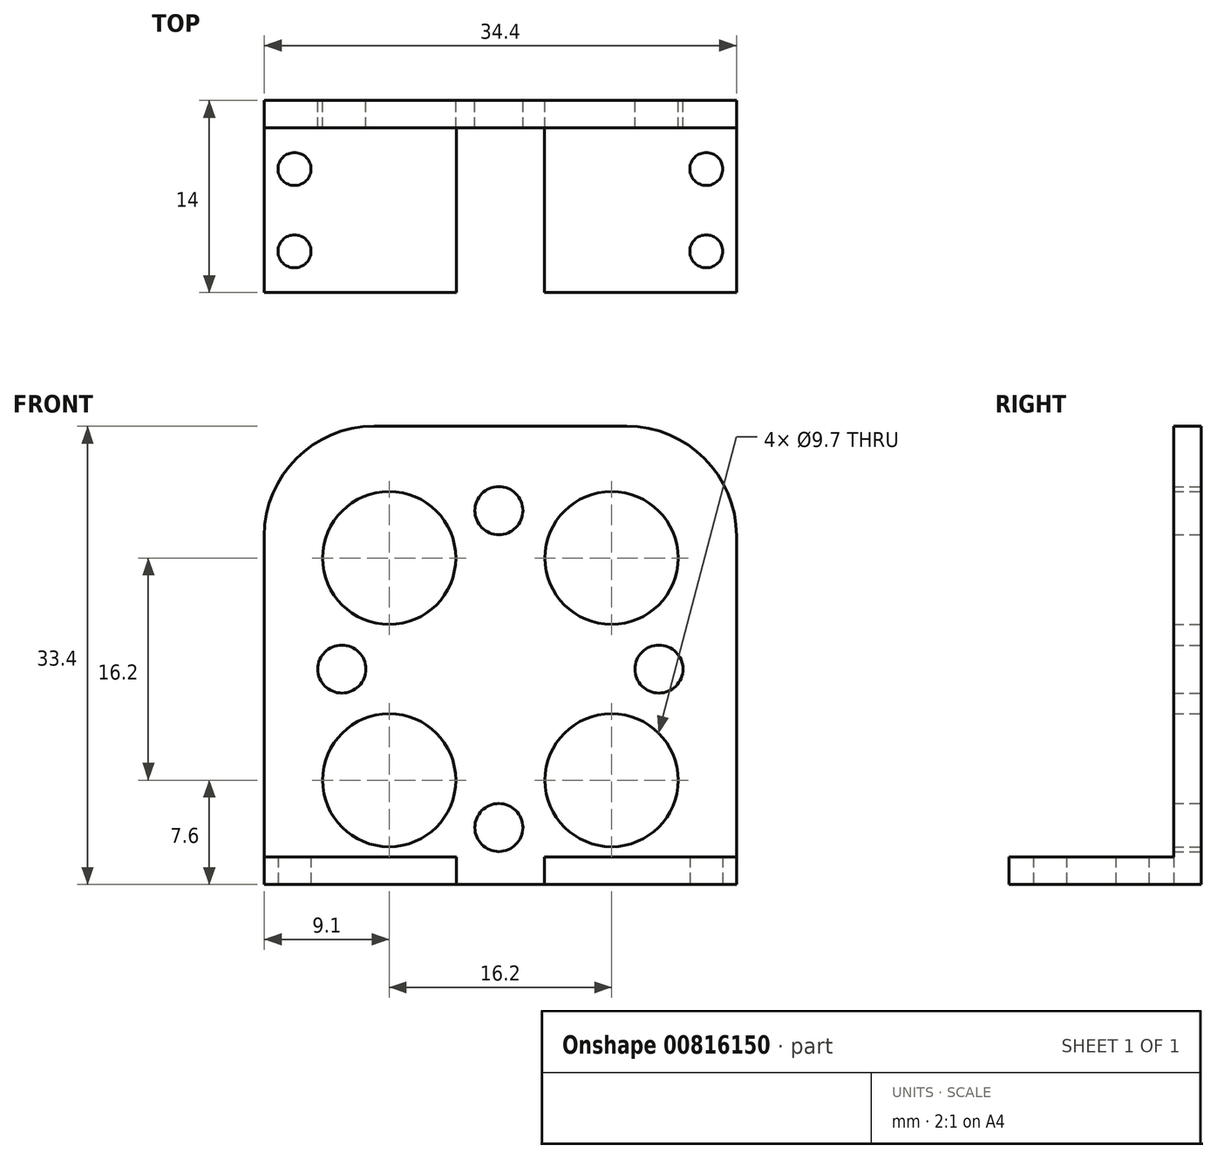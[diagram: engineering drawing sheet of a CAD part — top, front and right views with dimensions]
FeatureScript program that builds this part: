
annotation { "Feature Type Name" : "Feature", "Feature Type Description" : "" }
export const myFeature = defineFeature(function(context is Context, id is Id, definition is map)
    precondition{}
    {
        {
            var Q0;
            Q0=qCreatedBy(makeId("Front.planeOp"),FACE);
            var sketch = newSketch(context, id + "F0", { "sketchPlane" : qUnion([Q0])});
            skCircle(sketch, "E0", {"center": v(-0.11, 11.55) * mm, "radius": 1.75 * mm});
            skCircle(sketch, "E1", {"center": v(-11.55, 0) * mm, "radius": 1.75 * mm});
            skCircle(sketch, "E2", {"center": v(11.55, 0) * mm, "radius": 1.75 * mm});
            skCircle(sketch, "E3", {"center": v(-0.11, -11.55) * mm, "radius": 1.75 * mm});
            skLineSegment(sketch, "E4.bottom", {"start": v(-9.2, 17.7) * mm, "end": v(9.2, 17.7) * mm});
            skLineSegment(sketch, "E4.top", {"start": v(-17.2, -15.7) * mm, "end": v(17.2, -15.7) * mm});
            skLineSegment(sketch, "E4.left", {"start": v(-17.2, 9.7) * mm, "end": v(-17.2, -15.7) * mm});
            skLineSegment(sketch, "E4.right", {"start": v(17.2, 9.7) * mm, "end": v(17.2, -15.7) * mm});
            skCircle(sketch, "E5", {"center": v(-8.1, -8.1) * mm, "radius": 4.85 * mm});
            skCircle(sketch, "E6", {"center": v(-8.1, 8.1) * mm, "radius": 4.85 * mm});
            skCircle(sketch, "E7", {"center": v(8.1, 8.1) * mm, "radius": 4.85 * mm});
            skCircle(sketch, "E8", {"center": v(8.1, -8.1) * mm, "radius": 4.85 * mm});
            skPoint(sketch, "E9.visualSharp", {"position": v(-17.2, 17.7) * mm});
            skArc(sketch, "E9.filletArc", {"start": v(-9.2, 17.7) * mm, "mid": v(-14.86, 15.36) * mm, "end": v(-17.2, 9.7) * mm});
            skPoint(sketch, "E10.visualSharp", {"position": v(17.2, 17.7) * mm});
            skArc(sketch, "E10.filletArc", {"start": v(17.2, 9.7) * mm, "mid": v(14.86, 15.36) * mm, "end": v(9.2, 17.7) * mm});
            skSolve(sketch);
        }
        {
            var Q0;
            Q0=makeQuery(id+"F0.imprint","IMPRINT",FACE,{"disambiguationData":[TD([[makeQuery(id+"F0.imprint","IMPRINT",EDGE,{"derivedFrom":sQuery(id+"F0.wireOp",EDGE,"E0")}),-1.0]])]});
            var Q1;
            Q1 = qSketchRegion(id + "F2", true);
            extrude(context, id + "F1", {"entities" : qUnion([Q0, Q1]), "depth" : 2 * mm, "offsetDistance" : 25 * mm});
        }
        {
            var Q0;
            Q0=makeQuery(id+"F1.opExtrude","CAP_FACE",FACE,{"disambiguationData":[OSD([sQuery(id+"F0.wireOp",EDGE,"E0"),sQuery(id+"F0.wireOp",EDGE,"E1"),sQuery(id+"F0.wireOp",EDGE,"E2"),sQuery(id+"F0.wireOp",EDGE,"E3"),sQuery(id+"F0.wireOp",EDGE,"E4.bottom"),sQuery(id+"F0.wireOp",EDGE,"E4.top"),sQuery(id+"F0.wireOp",EDGE,"E4.left"),sQuery(id+"F0.wireOp",EDGE,"E4.right"),sQuery(id+"F0.wireOp",EDGE,"E5"),sQuery(id+"F0.wireOp",EDGE,"E6"),sQuery(id+"F0.wireOp",EDGE,"E7"),sQuery(id+"F0.wireOp",EDGE,"E8")])],"isStart":false});
            var sketch = newSketch(context, id + "F2", { "sketchPlane" : qUnion([Q0])});
            skLineSegment(sketch, "E11.bottom", {"start": v(-17.2, -13.7) * mm, "end": v(-3.2, -13.7) * mm});
            skLineSegment(sketch, "E11.top", {"start": v(-17.2, -15.7) * mm, "end": v(-3.2, -15.7) * mm});
            skLineSegment(sketch, "E11.left", {"start": v(-17.2, -13.7) * mm, "end": v(-17.2, -15.7) * mm});
            skLineSegment(sketch, "E11.right", {"start": v(-3.2, -13.7) * mm, "end": v(-3.2, -15.7) * mm});
            skLineSegment(sketch, "E12.bottom", {"start": v(17.2, -13.7) * mm, "end": v(3.2, -13.7) * mm});
            skLineSegment(sketch, "E12.top", {"start": v(17.2, -15.7) * mm, "end": v(3.2, -15.7) * mm});
            skLineSegment(sketch, "E12.left", {"start": v(17.2, -13.7) * mm, "end": v(17.2, -15.7) * mm});
            skLineSegment(sketch, "E12.right", {"start": v(3.2, -13.7) * mm, "end": v(3.2, -15.7) * mm});
            skSolve(sketch);
        }
        {
            var Q0;
            Q0=makeQuery(id+"F2.imprint","IMPRINT",FACE,{"disambiguationData":[TD([[makeQuery(id+"F2.imprint","IMPRINT",EDGE,{"derivedFrom":sQuery(id+"F2.wireOp",EDGE,"E11.bottom")}),-1.0]])]});
            var Q1;
            Q1=makeQuery(id+"F2.imprint","IMPRINT",FACE,{"disambiguationData":[TD([[makeQuery(id+"F2.imprint","IMPRINT",EDGE,{"derivedFrom":sQuery(id+"F2.wireOp",EDGE,"E12.bottom")}),1.0]])]});
            extrude(context, id + "F3", {"entities" : qUnion([Q0, Q1]), "operationType" : NewBodyOperationType.ADD, "depth" : 12 * mm, "offsetDistance" : 25 * mm});
        }
        {
            var Q0;
            Q0=makeQuery(id+"F3.boolean.opBoolean","MERGE",FACE,{"derivedFrom":[makeQuery(id+"F1.opExtrude","SWEPT_FACE",FACE,{"disambiguationData":[OSD([sQuery(id+"F0.wireOp",EDGE,"E4.top")])]}),makeQuery(id+"F3.opExtrude","SWEPT_FACE",FACE,{"disambiguationData":[OSD([sQuery(id+"F2.wireOp",EDGE,"E11.top")])]}),makeQuery(id+"F3.opExtrude","SWEPT_FACE",FACE,{"disambiguationData":[OSD([sQuery(id+"F2.wireOp",EDGE,"E12.top")])]})]});
            var sketch = newSketch(context, id + "F4", { "sketchPlane" : qUnion([Q0])});
            skCircle(sketch, "E13", {"center": v(-15, 11) * mm, "radius": 0.8 * mm});
            skCircle(sketch, "E14", {"center": v(15, 11) * mm, "radius": 0.8 * mm});
            skCircle(sketch, "E15", {"center": v(-15, 5) * mm, "radius": 0.8 * mm});
            skCircle(sketch, "E16", {"center": v(15, 5) * mm, "radius": 0.8 * mm});
            skSolve(sketch);
        }
        {
            var Q0;
            Q0=sQuery(id+"F4.wireOp",VERTEX,"E13.center");
            var Q1;
            Q1=sQuery(id+"F4.wireOp",VERTEX,"E15.center");
            var Q2;
            Q2=sQuery(id+"F4.wireOp",VERTEX,"E14.center");
            var Q3;
            Q3=sQuery(id+"F4.wireOp",VERTEX,"E16.center");
            var Q4;
            Q4=makeQuery(id+"F1.opExtrude","SWEPT_BODY",BODY,{"disambiguationData":[OSD([sQuery(id+"F0.wireOp",EDGE,"E0"),sQuery(id+"F0.wireOp",EDGE,"E1"),sQuery(id+"F0.wireOp",EDGE,"E2"),sQuery(id+"F0.wireOp",EDGE,"E3"),sQuery(id+"F0.wireOp",EDGE,"E4.bottom"),sQuery(id+"F0.wireOp",EDGE,"E4.top"),sQuery(id+"F0.wireOp",EDGE,"E4.left"),sQuery(id+"F0.wireOp",EDGE,"E4.right"),sQuery(id+"F0.wireOp",EDGE,"E5"),sQuery(id+"F0.wireOp",EDGE,"E6"),sQuery(id+"F0.wireOp",EDGE,"E7"),sQuery(id+"F0.wireOp",EDGE,"E8")])]});
            hole(context, id + "F5", {"style" : HoleStyle.SIMPLE, "endStyle" : HoleEndStyle.THROUGH, "holeDiameter" : 2.4 * mm, "majorDiameter" : 5 * mm, "isTappedThrough" : true, "tappedDepth" : 12 * mm, "tapClearance" : 3, "locations" : qUnion([Q0, Q1, Q2, Q3]), "scope" : qUnion([Q4])});
        }
    });
